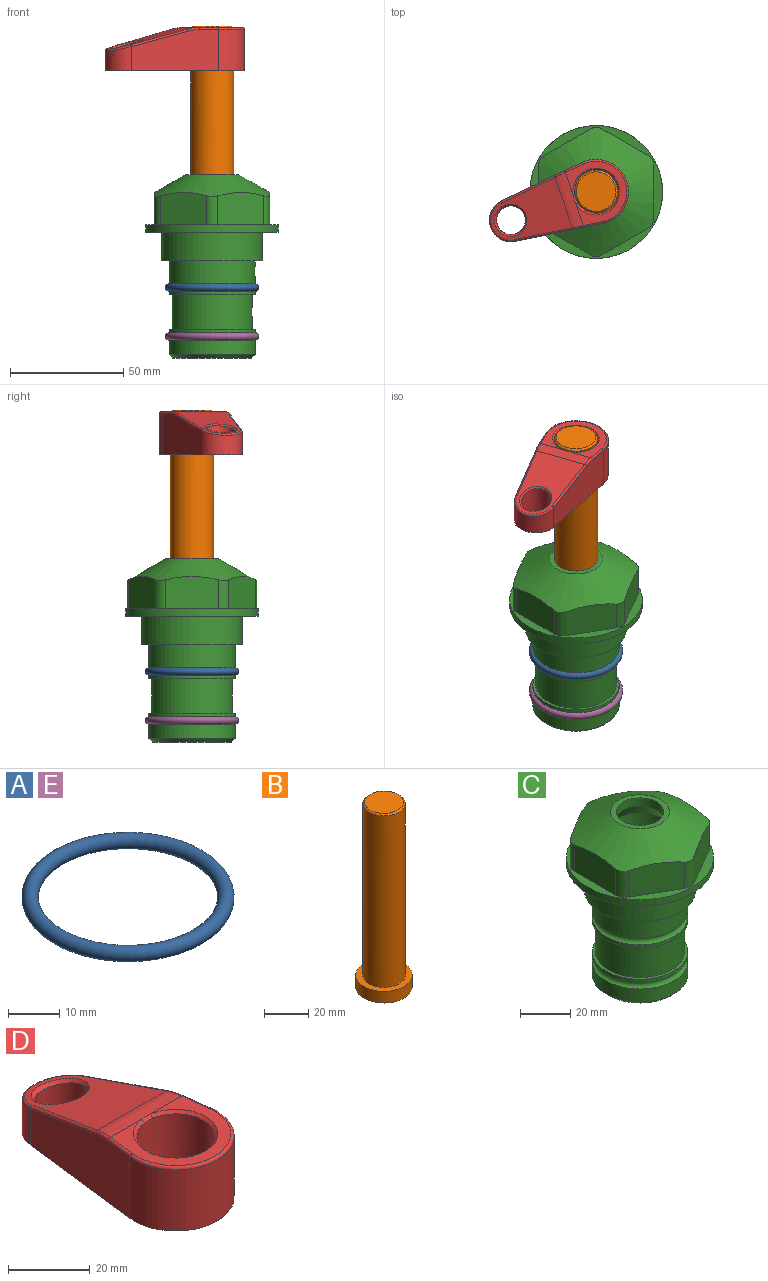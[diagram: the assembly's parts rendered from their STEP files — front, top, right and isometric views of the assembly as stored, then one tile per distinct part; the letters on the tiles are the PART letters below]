
ASSEMBLY  parts=5 mates=4
PART A: 1 faces, bbox 44.7x44.7x3.2 mm
  f0: torus R=19.05mm, axis (0,0,1), area 1193.9mm2
PART B: 6 faces, bbox 25.4x25.4x101.6 mm
  f0: plane 17.46x17.46mm, normal (0,0,1), area 239.5mm2, adj f5
  f1: plane 25.4x25.4mm, normal (0,0,-1), area 506.7mm2, adj f2
  f2: cylinder r=12.7mm len=25.4mm, axis (0,0,1), area 506.7mm2, adj f1,f3
  f3: plane 25.4x25.4mm, normal (0,0,1), area 221.7mm2, adj f2,f4
  f4: cylinder r=9.53mm len=94.46mm, axis (0,0,1), area 5653mm2, adj f3,f5
  f5: cone r=8.73mm half-angle=45deg, axis (0,0,-1), area 64.4mm2, adj f0,f4
PART C: 36 faces, bbox 58.7x58.7x81 mm
  f0: cylinder r=17.78mm len=35.56mm, axis (0,0,1), area 1670.8mm2, adj f23,f24,f31
  f1: cylinder r=19.05mm len=38.1mm, axis (0,0,1), area 1191.9mm2, adj f26,f27,f30
  f2: plane 58.66x58.66mm, normal (0,0,-1), area 1150.6mm2, adj f3,f28
  f3: cylinder r=29.33mm len=58.66mm, axis (0,0,-1), area 585.1mm2, adj f2,f4
  f4: plane 58.66x58.66mm, normal (0,0,1), area 475.9mm2, adj f3,f5,f6,f7,f8,f9,f10,f11
  f5: plane 20.32x14.34mm, normal (-0.5,0.87,0), area 324.4mm2, adj f4,f15,f16,f17
  f6: plane 20.32x14.34mm, normal (0.5,0.87,0), area 324.4mm2, adj f4,f14,f15,f17
  f7: plane 23.48x14.34mm, normal (1,0,0), area 324.4mm2, adj f4,f13,f14,f17
  f8: plane 20.32x14.34mm, normal (0.5,-0.87,0), area 324.4mm2, adj f4,f12,f13,f17
  f9: plane 20.32x14.34mm, normal (-0.5,-0.87,0), area 324.4mm2, adj f4,f11,f12,f17
  f10: plane 23.48x14.34mm, normal (-1,0,0), area 324.4mm2, adj f4,f11,f16,f17
  f11: cylinder r=5.08mm len=12.85mm, axis (0,0,-1), area 67.2mm2, adj f4,f9,f10,f17
  f12: cylinder r=5.08mm len=12.85mm, axis (0,0,-1), area 67.2mm2, adj f4,f8,f9,f17
  f13: cylinder r=5.08mm len=12.85mm, axis (0,0,-1), area 67.2mm2, adj f4,f7,f8,f17
  f14: cylinder r=5.08mm len=12.85mm, axis (0,0,-1), area 67.2mm2, adj f4,f6,f7,f17
  f15: cylinder r=5.08mm len=12.85mm, axis (0,0,-1), area 67.2mm2, adj f4,f5,f6,f17
  f16: cylinder r=5.08mm len=12.85mm, axis (0,0,-1), area 67.2mm2, adj f4,f5,f10,f17
  f17: cone r=11.73mm half-angle=60deg, axis (0,0,-1), area 2071.8mm2, adj f5,f6,f7,f8,f9,f10,f11,f12
  f18: plane 23.46x23.46mm, normal (0,0,1), area 147.4mm2, adj f17,f35
  f19: plane 34.93x34.93mm, normal (0,0,-1), area 958mm2, adj f29
  f20: cylinder r=19.05mm len=38.1mm, axis (0,0,1), area 760.1mm2, adj f21,f29
  f21: torus R=19.05mm, axis (0,0,1), area 565.3mm2, adj f20,f22
  f22: cylinder r=19.05mm len=38.1mm, axis (0,0,1), area 190mm2, adj f21,f23
  f23: plane 38.1x38.1mm, normal (0,0,1), area 146.9mm2, adj f0,f22
  f24: plane 38.1x38.1mm, normal (0,0,-1), area 146.9mm2, adj f0,f25
  f25: cylinder r=19.05mm len=38.1mm, axis (0,0,1), area 190mm2, adj f24,f26
  f26: torus R=19.05mm, axis (0,0,1), area 565.3mm2, adj f1,f25
  f27: plane 44.45x44.45mm, normal (0,0,-1), area 411.7mm2, adj f1,f28
  f28: cylinder r=22.23mm len=44.45mm, axis (0,0,1), area 1773.5mm2, adj f2,f27
  f29: cone r=19.05mm half-angle=45deg, axis (0,0,1), area 257.5mm2, adj f19,f20
  f30: cylinder r=3.17mm len=6.75mm, axis (-1,0,0), area 128mm2, adj f1,f33
  f31: cylinder r=3.17mm len=6.35mm, axis (-1,0,0), area 102.5mm2, adj f0,f33
  f32: plane 25.4x25.4mm, normal (0,0,1), area 506.7mm2, adj f33
  f33: cylinder r=12.7mm len=66.42mm, axis (0,0,-1), area 5236.2mm2, adj f30,f31,f32,f34
  f34: cone r=9.53mm half-angle=30deg, axis (0,0,-1), area 443.4mm2, adj f33,f35
  f35: cylinder r=9.53mm len=19.05mm, axis (0,0,-1), area 240.9mm2, adj f18,f34
PART D: 31 faces, bbox 31.7x65.5x19.8 mm
  f0: plane 39.12x18.26mm, normal (0.99,0.12,0), area 612.2mm2, adj f1,f4,f7,f11,f13,f15
  f1: cylinder r=9.53mm len=18.91mm, axis (0,0,-1), area 296.1mm2, adj f0,f2,f7,f17
  f2: plane 39.12x18.26mm, normal (-0.99,0.12,0), area 612.2mm2, adj f1,f4,f7,f12,f14,f16
  f3: cylinder r=6.35mm len=12.7mm, axis (0,0,-1), area 362.4mm2, adj f7,f18
  f4: cylinder r=14.29mm len=28.58mm, axis (0,0,-1), area 882.2mm2, adj f0,f2,f7,f10
  f5: cylinder r=9.53mm len=19.05mm, axis (0,0,-1), area 1092.6mm2, adj f7,f19,f20
  f6: plane 26.99x23.69mm, normal (0,0,1), area 216.2mm2, adj f9,f10,f11,f12,f19
  f7: plane 63.5x28.58mm, normal (0,0,-1), area 661.8mm2, adj f0,f1,f2,f3,f4,f5,f22,f23
  f8: plane 33.52x23.6mm, normal (0,0.26,0.97), area 486mm2, adj f9,f15,f16,f17,f18
  f9: cylinder r=19.05mm len=24.72mm, axis (1,0,0), area 120.4mm2, adj f6,f8,f13,f14,f20
  f10: torus R=13.49mm, axis (0,0,1), area 59mm2, adj f4,f6,f11,f12
  f11: cylinder r=0.79mm len=8.67mm, axis (0.12,-0.99,0), area 10.8mm2, adj f0,f6,f10,f13
  f12: cylinder r=0.79mm len=8.67mm, axis (0.12,0.99,0), area 10.8mm2, adj f2,f6,f10,f14
  f13: bspline ~4.95x1.42mm, area 6.1mm2, adj f0,f9,f11,f15
  f14: bspline ~4.95x1.42mm, area 6.1mm2, adj f2,f9,f12,f16
  f15: cylinder r=0.79mm len=25.95mm, axis (0.12,-0.96,0.26), area 32.9mm2, adj f0,f8,f13,f17
  f16: cylinder r=0.79mm len=25.95mm, axis (0.12,0.96,-0.26), area 32.9mm2, adj f2,f8,f14,f17
  f17: bspline ~18.91x8.38mm, area 30mm2, adj f1,f8,f15,f16
  f18: bspline ~14.29x14.29mm, area 48.3mm2, adj f3,f8
  f19: cone r=9.53mm half-angle=45deg, axis (0,0,1), area 66.5mm2, adj f5,f6,f20
  f20: bspline ~3.22x0.96mm, area 3.5mm2, adj f5,f9,f19
  f21: plane 2.75x2.72mm, normal (0,0,-1), area 2.9mm2, adj f23,f25,f28
  f22: plane 23.05x15.88mm, normal (-0.99,-0.12,0), area 323.6mm2, adj f7,f25,f26,f27,f28,f29
  f23: plane 23.05x15.88mm, normal (0.99,-0.12,0), area 323.6mm2, adj f7,f21,f25,f27,f28,f30
  f24: cylinder r=9.53mm len=10.69mm, axis (0,0,-1), area 114.7mm2, adj f7,f27,f29,f30
  f25: cylinder r=12.7mm len=20.59mm, axis (0,0,-1), area 381.1mm2, adj f7,f21,f22,f23,f26,f28
  f26: plane 2.75x2.72mm, normal (0,0,-1), area 2.9mm2, adj f22,f25,f28
  f27: plane 19.72x18.37mm, normal (0,-0.26,-0.97), area 291.8mm2, adj f22,f23,f24,f28,f29,f30
  f28: cylinder r=15.88mm len=19.92mm, axis (1,0,0), area 54.8mm2, adj f21,f22,f23,f25,f26,f27
  f29: cylinder r=1.59mm len=11mm, axis (0,0,-1), area 34.7mm2, adj f7,f22,f24,f27
  f30: cylinder r=1.59mm len=11mm, axis (0,0,-1), area 34.7mm2, adj f7,f23,f24,f27
PART E: same geometry as A
PLACE A at identity
PLACE B rot(axis=(0,0,1),108.5deg) t=(0,0,27.55)mm
PLACE C at identity fixed
PLACE D rot(axis=(0,0,1),108.5deg) t=(0,0,26.76)mm
PLACE E t=(0,0,-21.59)mm
MATE cylindrical C.f0 <-> B.f2  axis (0,0,1) through (0,0,-50.55)mm
MATE fastened C.f0 <-> A.f0  axis (0,0,1) through (0,0,-24.51)mm
MATE fastened B.f2 <-> D.f4  axis (0,0,-1) through (0,0,90.26)mm
MATE fastened C.f0 <-> E.f0  axis (0,0,1) through (0,0,-46.1)mm
